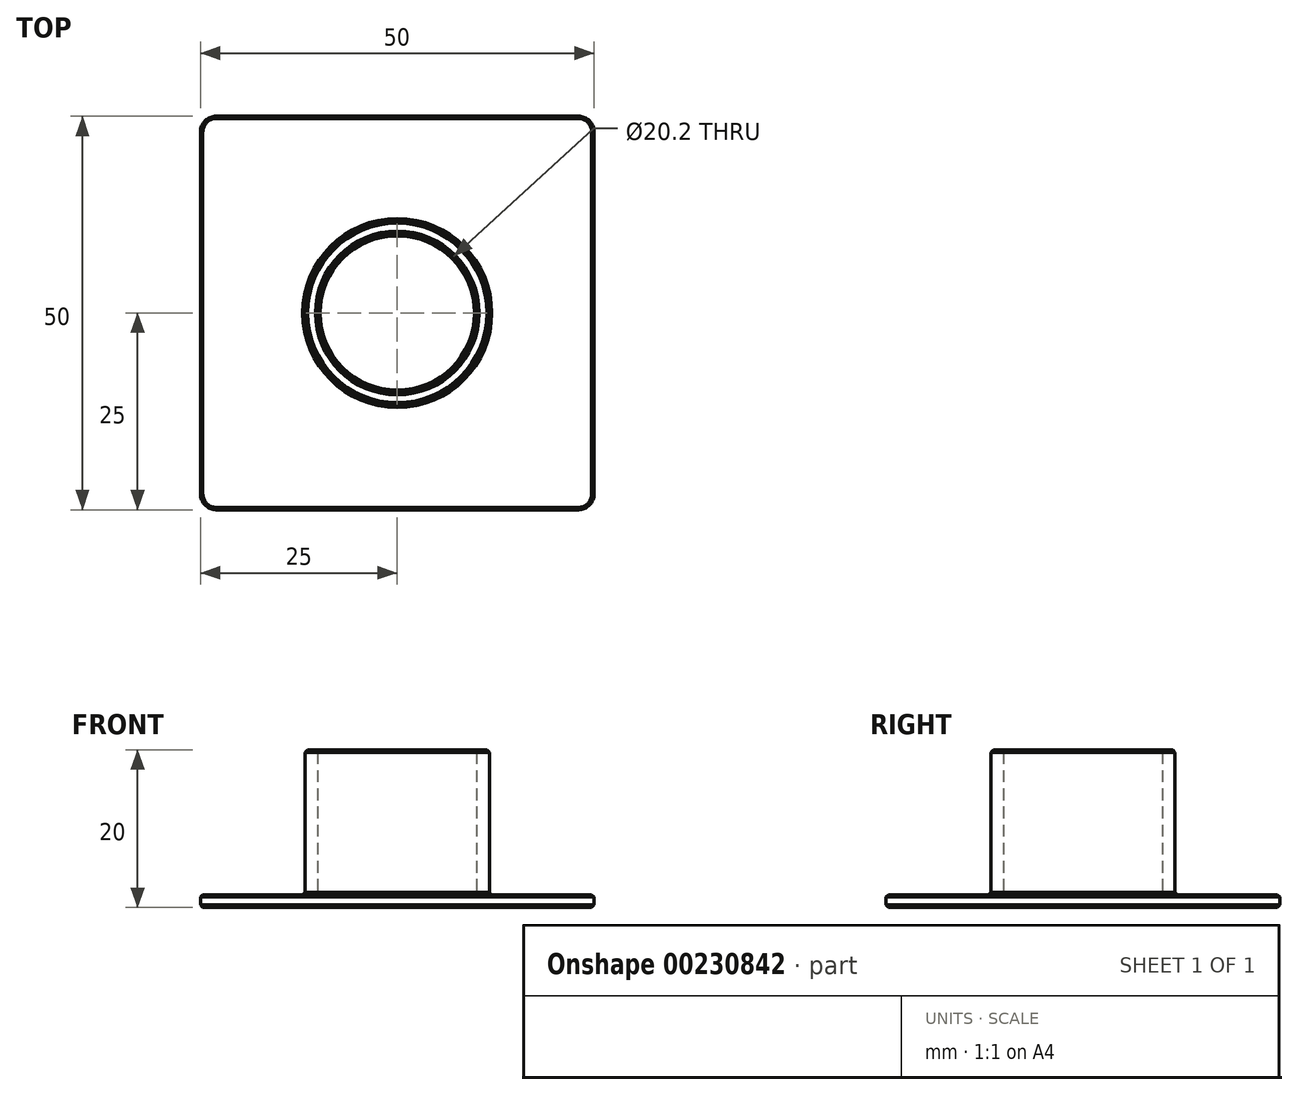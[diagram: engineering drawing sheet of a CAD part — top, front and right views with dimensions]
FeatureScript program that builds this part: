
annotation { "Feature Type Name" : "Feature", "Feature Type Description" : "" }
export const myFeature = defineFeature(function(context is Context, id is Id, definition is map)
    precondition{}
    {
        {
            assignVariable(context, id + "F0", {"name" : "wallthickness", "anyValue" : 1.6});
        }
        {
            var Q0;
            Q0=qCreatedBy(makeId("Top.planeOp"),FACE);
            var sketch = newSketch(context, id + "F1", { "sketchPlane" : qUnion([Q0])});
            skCircle(sketch, "E0", {"center": v(0, 0) * mm, "radius": 10.1 * mm});
            skCircle(sketch, "E1.0", {"center": v(0, 0) * mm, "radius": 11.7 * mm});
            skLineSegment(sketch, "E2.bottom", {"start": v(-25, 25) * mm, "end": v(25, 25) * mm});
            skLineSegment(sketch, "E2.top", {"start": v(-25, -25) * mm, "end": v(25, -25) * mm});
            skLineSegment(sketch, "E2.left", {"start": v(-25, 25) * mm, "end": v(-25, -25) * mm});
            skLineSegment(sketch, "E2.right", {"start": v(25, 25) * mm, "end": v(25, -25) * mm});
            skSolve(sketch);
        }
        {
            var Q0;
            Q0 = qSketchRegion(id + "F1", true);
            var Q1;
            Q1=makeQuery(id+"F1.imprint","IMPRINT",FACE,{"disambiguationData":[TD([[makeQuery(id+"F1.imprint","IMPRINT",EDGE,{"derivedFrom":sQuery(id+"F1.wireOp",EDGE,"E0")}),-1.0]])]});
            var Q2;
            Q2=makeQuery(id+"F1.imprint","IMPRINT",FACE,{"disambiguationData":[TD([[makeQuery(id+"F1.imprint","IMPRINT",EDGE,{"derivedFrom":sQuery(id+"F1.wireOp",EDGE,"E0")}),1.0]])]});
            extrude(context, id + "F2", {"entities" : qUnion([Q0, Q1, Q2]), "depth" : (getVariable(context, 'wallthickness')) * mm});
        }
        {
            var Q0;
            Q0=makeQuery(id+"F1.imprint","IMPRINT",FACE,{"disambiguationData":[TD([[makeQuery(id+"F1.imprint","IMPRINT",EDGE,{"derivedFrom":sQuery(id+"F1.wireOp",EDGE,"E0")}),-1.0]])]});
            extrude(context, id + "F5", {"entities" : qUnion([Q0]), "operationType" : NewBodyOperationType.ADD, "depth" : 20 * mm});
        }
        {
            var Q0;
            Q0=makeQuery(id+"F2.opExtrude","SWEPT_EDGE",EDGE,{"disambiguationData":[OSD([sQuery(id+"F1.wireOp",EDGE,"E2.bottom"),sQuery(id+"F1.wireOp",EDGE,"E2.right")])]});
            var Q1;
            Q1=makeQuery(id+"F2.opExtrude","SWEPT_EDGE",EDGE,{"disambiguationData":[OSD([sQuery(id+"F1.wireOp",EDGE,"E2.top"),sQuery(id+"F1.wireOp",EDGE,"E2.right")])]});
            var Q2;
            Q2=makeQuery(id+"F2.opExtrude","SWEPT_EDGE",EDGE,{"disambiguationData":[OSD([sQuery(id+"F1.wireOp",EDGE,"E2.top"),sQuery(id+"F1.wireOp",EDGE,"E2.left")])]});
            var Q3;
            Q3=makeQuery(id+"F2.opExtrude","SWEPT_EDGE",EDGE,{"disambiguationData":[OSD([sQuery(id+"F1.wireOp",EDGE,"E2.bottom"),sQuery(id+"F1.wireOp",EDGE,"E2.left")])]});
            fillet(context, id + "F3", {"entities" : qUnion([Q0, Q1, Q2, Q3]), "radius" : 2 * mm, "tangentPropagation" : true, "allowEdgeOverflow" : false});
        }
        {
            var Q0;
            Q0=makeQuery(id+"F2.opExtrude","CAP_FACE",FACE,{"disambiguationData":[OSD([sQuery(id+"F1.wireOp",EDGE,"E1.0"),sQuery(id+"F1.wireOp",EDGE,"E2.bottom"),sQuery(id+"F1.wireOp",EDGE,"E2.top"),sQuery(id+"F1.wireOp",EDGE,"E2.left"),sQuery(id+"F1.wireOp",EDGE,"E2.right")])],"isStart":false});
            var Q1;
            {var subQ0=sQuery(id+"F1.wireOp",EDGE,"E1.0");Q1=makeQuery(id+"F5.boolean.opBoolean","MERGE",FACE,{"derivedFrom":[makeQuery(id+"F2.opExtrude","CAP_FACE",FACE,{"disambiguationData":[OSD([subQ0,sQuery(id+"F1.wireOp",EDGE,"E2.bottom"),sQuery(id+"F1.wireOp",EDGE,"E2.top"),sQuery(id+"F1.wireOp",EDGE,"E2.left"),sQuery(id+"F1.wireOp",EDGE,"E2.right")])],"isStart":true}),makeQuery(id+"F5.opExtrude","CAP_FACE",FACE,{"disambiguationData":[OSD([sQuery(id+"F1.wireOp",EDGE,"E0"),subQ0])],"isStart":true})]});}
            var Q2;
            Q2=makeQuery(id+"F5.opExtrude","CAP_EDGE",EDGE,{"disambiguationData":[OSD([sQuery(id+"F1.wireOp",EDGE,"E0")])],"isStart":false});
            var Q3;
            Q3=makeQuery(id+"F5.opExtrude","CAP_EDGE",EDGE,{"disambiguationData":[OSD([sQuery(id+"F1.wireOp",EDGE,"E1.0")])],"isStart":false});
            chamfer(context, id + "F4", {"entities" : qUnion([Q0, Q1, Q2, Q3]), "width" : 0.3 * mm, "tangentPropagation" : true});
        }
    });
